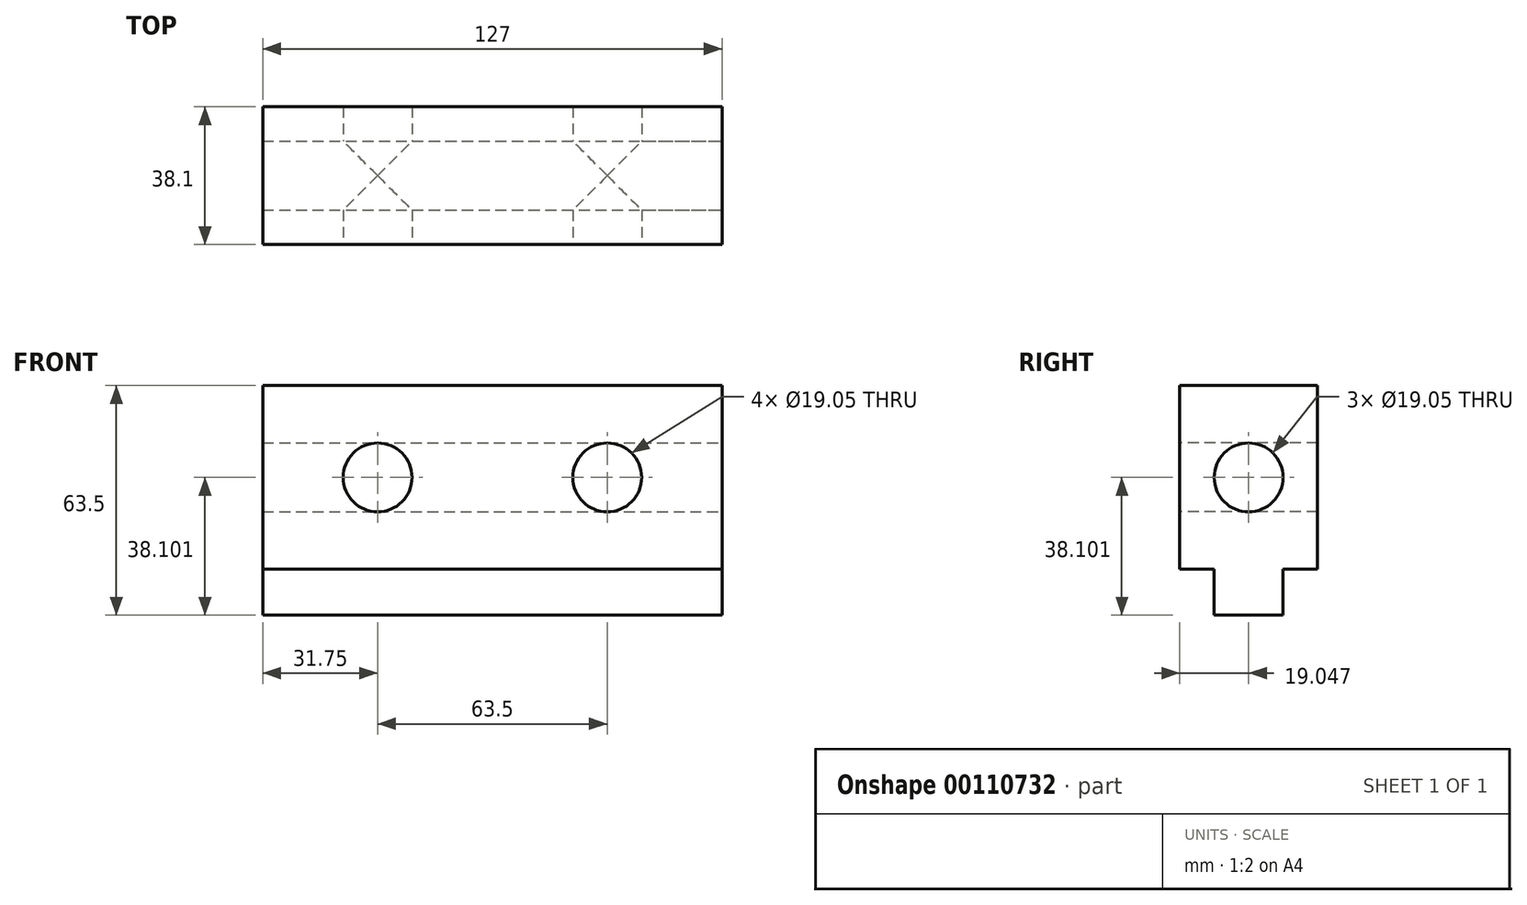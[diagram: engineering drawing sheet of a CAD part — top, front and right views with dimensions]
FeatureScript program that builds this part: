
annotation { "Feature Type Name" : "Feature", "Feature Type Description" : "" }
export const myFeature = defineFeature(function(context is Context, id is Id, definition is map)
    precondition{}
    {
        {
            var Q0;
            Q0=qCreatedBy(makeId("Right.planeOp"),FACE);
            var sketch = newSketch(context, id + "F0", { "sketchPlane" : qUnion([Q0])});
            skLineSegment(sketch, "E0", {"start": v(-20.98, -11.49) * mm, "end": v(-20.98, -24.19) * mm});
            skLineSegment(sketch, "E1", {"start": v(-20.98, -24.19) * mm, "end": v(-40.03, -24.19) * mm});
            skLineSegment(sketch, "E2", {"start": v(-40.03, -24.19) * mm, "end": v(-40.03, -11.49) * mm});
            skLineSegment(sketch, "E3", {"start": v(-40.03, -11.49) * mm, "end": v(-49.55, -11.49) * mm});
            skLineSegment(sketch, "E4", {"start": v(-49.55, -11.49) * mm, "end": v(-49.55, 39.31) * mm});
            skLineSegment(sketch, "E5", {"start": v(-49.55, 39.31) * mm, "end": v(-11.45, 39.31) * mm});
            skLineSegment(sketch, "E6", {"start": v(-11.45, 39.31) * mm, "end": v(-11.45, -11.49) * mm});
            skLineSegment(sketch, "E7", {"start": v(-11.45, -11.49) * mm, "end": v(-20.98, -11.49) * mm});
            skSolve(sketch);
        }
        {
            var Q0;
            Q0=makeQuery(id+"F0.imprint","IMPRINT",FACE,{"disambiguationData":[TD([[makeQuery(id+"F0.imprint","IMPRINT",EDGE,{"derivedFrom":sQuery(id+"F0.wireOp",EDGE,"E0")}),-1.0]])]});
            extrude(context, id + "F1", {"entities" : qUnion([Q0]), "oppositeDirection" : true, "depth" : 127 * mm});
        }
        {
            var Q0;
            Q0=makeQuery(id+"F1.opExtrude","CAP_FACE",FACE,{"disambiguationData":[OSD([sQuery(id+"F0.wireOp",EDGE,"E0"),sQuery(id+"F0.wireOp",EDGE,"E1"),sQuery(id+"F0.wireOp",EDGE,"E2"),sQuery(id+"F0.wireOp",EDGE,"E3"),sQuery(id+"F0.wireOp",EDGE,"E4"),sQuery(id+"F0.wireOp",EDGE,"E5"),sQuery(id+"F0.wireOp",EDGE,"E6"),sQuery(id+"F0.wireOp",EDGE,"E7")])],"isStart":true});
            var sketch = newSketch(context, id + "F2", { "sketchPlane" : qUnion([Q0])});
            skCircle(sketch, "E8", {"center": v(-30.5, 13.91) * mm, "radius": 9.53 * mm});
            skSolve(sketch);
        }
        {
            var Q0;
            Q0 = qSketchRegion(id + "F2", true);
            extrude(context, id + "F3", {"entities" : qUnion([Q0]), "operationType" : NewBodyOperationType.REMOVE, "endBound" : BoundingType.THROUGH_ALL, "oppositeDirection" : true, "depth" : 25.4 * mm});
        }
        {
            var Q0;
            Q0=makeQuery(id+"F1.opExtrude","SWEPT_FACE",FACE,{"disambiguationData":[OSD([sQuery(id+"F0.wireOp",EDGE,"E4")])]});
            var sketch = newSketch(context, id + "F4", { "sketchPlane" : qUnion([Q0])});
            skCircle(sketch, "E9", {"center": v(-95.25, 13.91) * mm, "radius": 9.53 * mm});
            skCircle(sketch, "E10", {"center": v(-31.75, 13.91) * mm, "radius": 9.53 * mm});
            skSolve(sketch);
        }
        {
            var Q0;
            Q0 = qSketchRegion(id + "F4", true);
            extrude(context, id + "F5", {"entities" : qUnion([Q0]), "operationType" : NewBodyOperationType.REMOVE, "endBound" : BoundingType.THROUGH_ALL, "oppositeDirection" : true, "depth" : 25.4 * mm});
        }
    });
